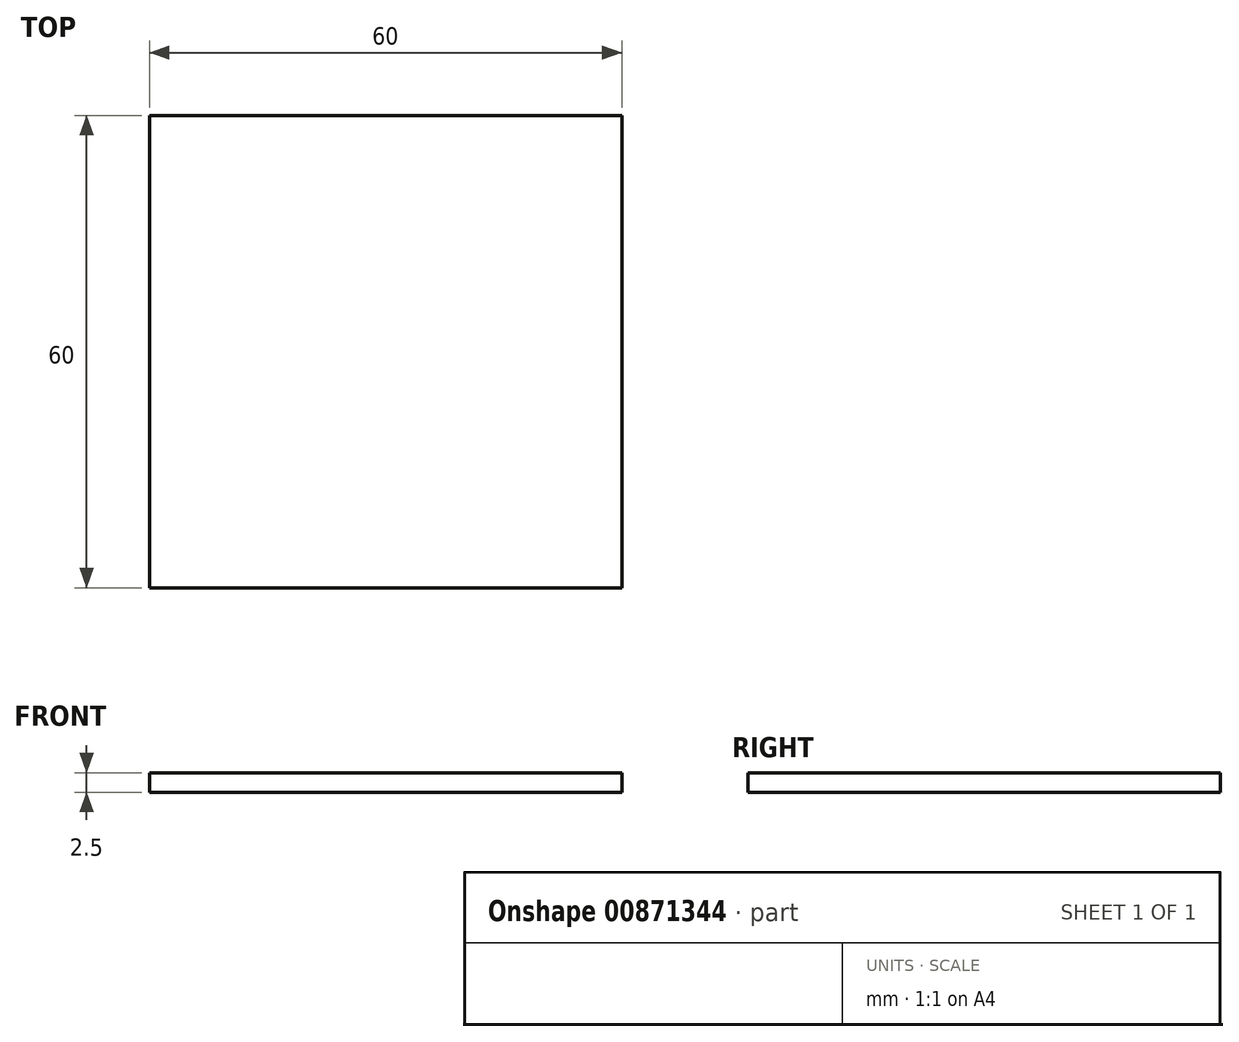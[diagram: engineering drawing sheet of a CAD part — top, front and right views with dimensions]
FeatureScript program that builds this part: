
annotation { "Feature Type Name" : "Feature", "Feature Type Description" : "" }
export const myFeature = defineFeature(function(context is Context, id is Id, definition is map)
    precondition{}
    {
        {
            var Q0;
            Q0=qCreatedBy(makeId("Top.planeOp"),FACE);
            var sketch = newSketch(context, id + "F0", { "sketchPlane" : qUnion([Q0])});
            skLineSegment(sketch, "E0", {"start": v(-21.29, 35.7) * mm, "end": v(38.71, 35.7) * mm});
            skLineSegment(sketch, "E1", {"start": v(38.71, 35.7) * mm, "end": v(38.71, -24.3) * mm});
            skLineSegment(sketch, "E2", {"start": v(38.71, -24.3) * mm, "end": v(-21.29, -24.3) * mm});
            skLineSegment(sketch, "E3", {"start": v(-21.29, -24.3) * mm, "end": v(-21.29, 35.7) * mm});
            skSolve(sketch);
        }
        {
            var Q0;
            Q0=makeQuery(id+"F0.imprint","IMPRINT",FACE,{"disambiguationData":[TD([[makeQuery(id+"F0.imprint","IMPRINT",EDGE,{"derivedFrom":sQuery(id+"F0.wireOp",EDGE,"E0")}),-1.0]])]});
            extrude(context, id + "F1", {"entities" : qUnion([Q0]), "depth" : 2.5 * mm, "offsetDistance" : 25 * mm});
        }
    });
